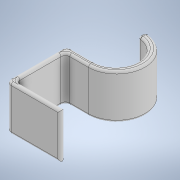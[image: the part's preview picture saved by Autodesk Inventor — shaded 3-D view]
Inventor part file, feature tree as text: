
AUTODESK INVENTOR PART (.ipt)
format: ipt  version: 2020 (Build 240168000, 168)  size: 222,720 bytes
history: native  units: in
note: dims shown in document units (in); Inventor stores cm internally (conversion verified against a paired STEP export)
features: fillet x3, extrude x1, sketch x1
ambient origin geometry x8: Origin, YZ Plane, XZ Plane, XY Plane, X Axis, Y Axis, Z Axis, Center Point
bodies: Solid1 (feature_tree)
feature tree (5):
  extrude  "Extrusion1"  Depth=0.0787in
  fillet  "Fillet1"  Radius=0.1181in
  fillet  "Fillet2"  Radius=0.0787in
  fillet  "Fillet3"  Radius=0.9449in
  sketch  "Sketch1"  dims[d0=0.8661in d1=0.0787in d2=0.1181in d3=0.0787in d4=0.9449in d5=0.4724in d6=0.3937in d7=0.7874in d8=0.3937in d9=0.1181in d10=0.1181in d11=0.1181in d12=0.7874in d13=0.0in d14=0.0787in d15=0.0394in d16=0.0591in]
